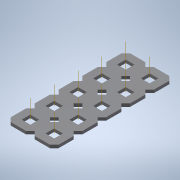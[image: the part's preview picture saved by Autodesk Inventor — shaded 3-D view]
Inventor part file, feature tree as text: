
AUTODESK INVENTOR PART (.ipt)
format: ipt  version: 2020 (Build 240168000, 168)  size: 1,143,808 bytes
history: native  units: in
note: dims shown in document units (in); Inventor stores cm internally (conversion verified against a paired STEP export)
features: other x19, extrude x2, pattern_linear x1, plane x1, split x1, imported_body x1
ambient origin geometry x8: Origin, YZ Plane, XZ Plane, XY Plane, X Axis, Y Axis, Z Axis, Center Point
bodies: Body1 (feature_tree)
feature tree (25):
  other  "Diamond-Pattern"
  other  "Plate"
  extrude  "length cut"  TaperAngle=0.0deg  [1 undecoded]
  extrude  "width cut"  TaperAngle=0.0deg  [1 undecoded]
  other  "constraint axis"
  pattern_linear  "constraint axes"  Spacing1=0.5in  [1 undecoded]
  other  "front plane"
  other  "right plane"
  plane  "Work Plane5"
  split  "Split1"
  imported_body  "Base1"
  other  "length profile"
  other  "width profile"
  other  "Work Point1"
  other  "Work Axis36"
  other  "Work Axis37"
  other  "Work Axis38"
  other  "Work Axis40"
  other  "Work Axis42"
  other  "Work Axis44"
  other  "Work Axis46"
  other  "back plane"
  other  "left plane"
  other  "Work Axis170"
  other  "Work Axis171"
note: 3 required parameter values undecoded (feature->parameter linkage not recoverable at this tier; creation-order binding heuristic only, values carry confidence <= 0.55)
